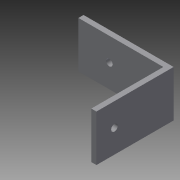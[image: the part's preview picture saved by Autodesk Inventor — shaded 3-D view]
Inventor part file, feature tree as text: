
AUTODESK INVENTOR PART (.ipt)
format: ipt  version: 2015 (Build 190159000, 159)  size: 95,232 bytes
history: native  units: in
note: dims shown in document units (in); Inventor stores cm internally (conversion verified against a paired STEP export)
features: sketch x4, extrude x3, hole x1, projected_geometry x1
ambient origin geometry x8: Origin, YZ Plane, XZ Plane, XY Plane, X Axis, Y Axis, Z Axis, Center Point
bodies: Solid1 (feature_tree)
feature tree (9):
  extrude  "Extrusion1"  Depth=1.75in
  extrude  "Extrusion2"  Depth=0.1in
  hole  "Hole2"  [1 undecoded]
  extrude  "Extrusion3"  Depth=0.05in
  sketch  "Sketch1"  dims[d0=0.9in d1=1.75in]
  sketch  "Sketch2"  dims[d2=0.1in d3=0.0in d4=0.1in]
  sketch  "Sketch4"  dims[d5=1.4in d6=0.0in d16=0.45in]
  projected_geometry  "Projected Loop2"
  sketch  "Sketch5"  dims[d17=1.05in d18=0.128in d19=0.75in d20=0.375in d21=0.25in d22=0.5635in d23=1.0in d24=0.8108in d25=0.05in d26=1.0in d27=0.0in]
note: 1 required parameter value undecoded (feature->parameter linkage not recoverable at this tier; creation-order binding heuristic only, values carry confidence <= 0.55)
